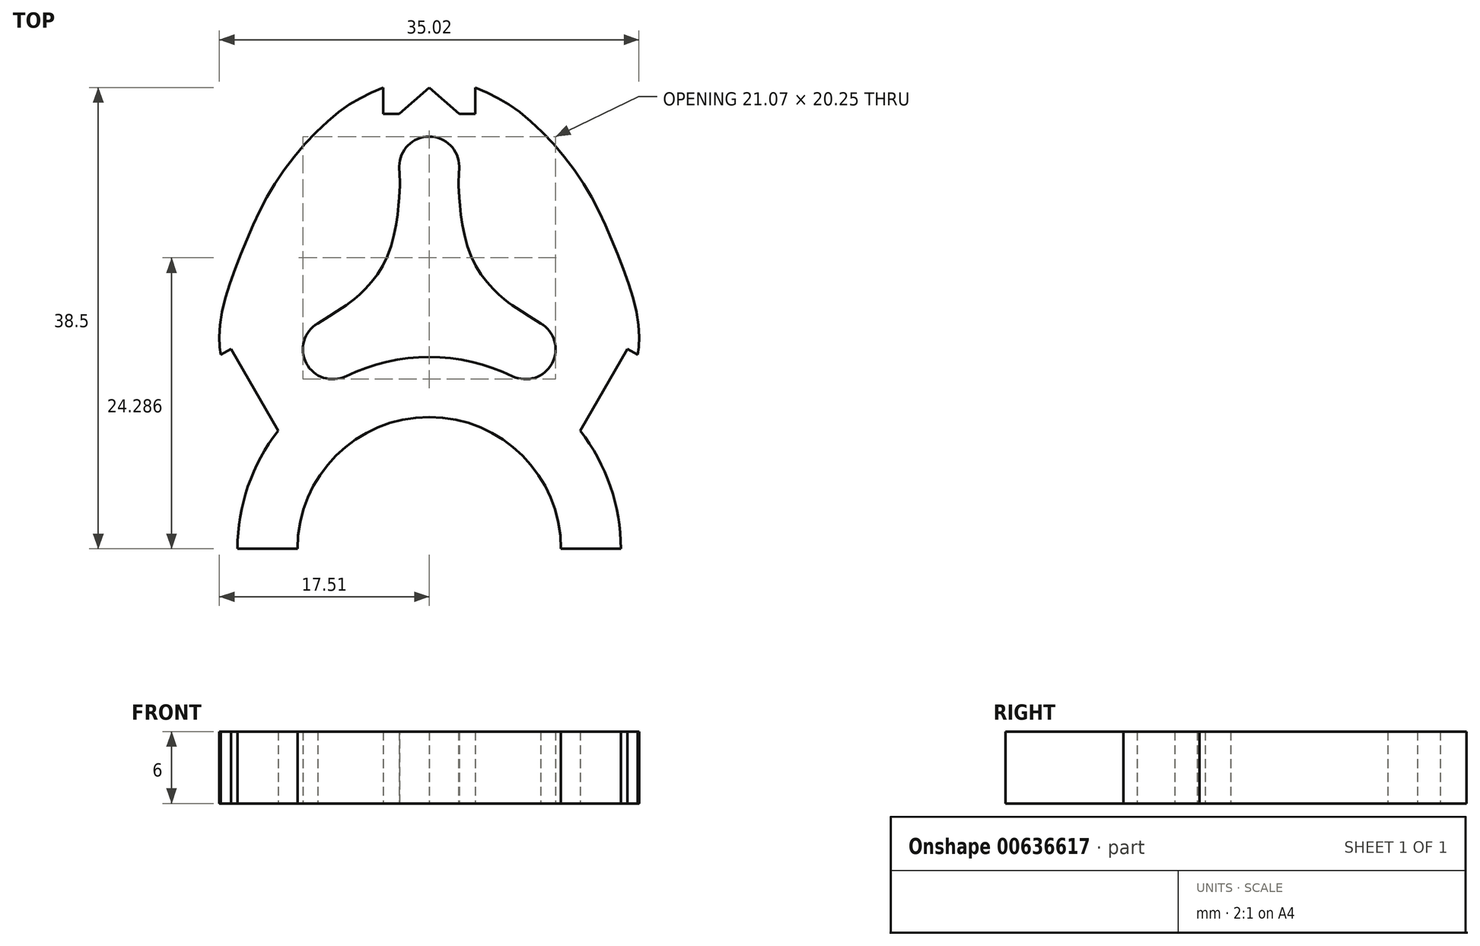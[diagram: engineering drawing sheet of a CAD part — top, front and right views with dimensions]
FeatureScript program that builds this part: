
annotation { "Feature Type Name" : "Feature", "Feature Type Description" : "" }
export const myFeature = defineFeature(function(context is Context, id is Id, definition is map)
    precondition{}
    {
        {
            var Q0;
            Q0=qCreatedBy(makeId("Top.planeOp"),FACE);
            var sketch = newSketch(context, id + "F0", { "sketchPlane" : qUnion([Q0])});
            skArc(sketch, "E0", {"start": v(16, 0) * mm, "mid": v(15.13, 5.21) * mm, "end": v(12.6, 9.86) * mm});
            skArc(sketch, "E1", {"start": v(11, 0) * mm, "mid": v(0, 11) * mm, "end": v(-11, 0) * mm});
            skLineSegment(sketch, "E2", {"start": v(0, 36.3) * mm, "end": v(0, 0) * mm, "construction": true});
            skLineSegment(sketch, "E3", {"start": v(3.84, 36.3) * mm, "end": v(2.52, 36.3) * mm});
            skLineSegment(sketch, "E4", {"start": v(16.55, 16.69) * mm, "end": v(17.41, 16.19) * mm});
            skFitSpline(sketch, "E5", {"points": [v(17.41, 16.19) * mm, v(17.41, 19.08) * mm, v(15.54, 25.05) * mm, v(12.52, 31.03) * mm, v(7.74, 36.3) * mm, v(3.84, 38.5) * mm], "startDerivative": vector(1.86, 12.58) * mm, "endDerivative": vector(-23.54, 9.7) * mm});
            skLineSegment(sketch, "E6", {"start": v(3.84, 38.5) * mm, "end": v(3.84, 36.3) * mm});
            skLineSegment(sketch, "E7.MirrorCS", {"start": v(-3.84, 36.3) * mm, "end": v(-2.52, 36.3) * mm});
            skLineSegment(sketch, "E8.MirrorCS", {"start": v(-16.55, 16.69) * mm, "end": v(-17.41, 16.19) * mm});
            skLineSegment(sketch, "E9.MirrorCS", {"start": v(-3.84, 38.5) * mm, "end": v(-3.84, 36.3) * mm});
            skFitSpline(sketch, "E10.MirrorCS", {"points": [v(-17.41, 16.19) * mm, v(-17.41, 19.08) * mm, v(-15.54, 25.05) * mm, v(-12.52, 31.03) * mm, v(-7.74, 36.3) * mm, v(-3.84, 38.5) * mm], "startDerivative": vector(-1.86, 12.58) * mm, "endDerivative": vector(23.54, 9.7) * mm});
            skLineSegment(sketch, "E11", {"start": v(-2.52, 36.3) * mm, "end": v(0, 38.5) * mm});
            skLineSegment(sketch, "E12.MirrorCS", {"start": v(2.52, 36.3) * mm, "end": v(0, 38.5) * mm});
            skArc(sketch, "E13", {"start": v(2.5, 31.9) * mm, "mid": v(0, 34.4) * mm, "end": v(-2.5, 31.9) * mm});
            skArc(sketch, "E14", {"start": v(-9.3, 18.82) * mm, "mid": v(-10.26, 15.48) * mm, "end": v(-6.96, 14.4) * mm});
            skArc(sketch, "E15.MirrorC", {"start": v(9.3, 18.82) * mm, "mid": v(10.26, 15.48) * mm, "end": v(6.96, 14.4) * mm});
            skCircle(sketch, "E16", {"center": v(0, 21.92) * mm, "radius": 3 * mm, "construction": true});
            skFitSpline(sketch, "E17", {"points": [v(-2.5, 31.9) * mm, v(-2.49, 29.65) * mm, v(-3.62, 24.11) * mm, v(-6.5, 20.64) * mm, v(-9.3, 18.82) * mm], "startDerivative": vector(1.05, -19.69) * mm, "endDerivative": vector(-25.78, -16.42) * mm});
            skFitSpline(sketch, "E18.MirrorCS", {"points": [v(2.5, 31.9) * mm, v(2.49, 29.65) * mm, v(3.62, 24.11) * mm, v(6.5, 20.64) * mm, v(9.3, 18.82) * mm], "startDerivative": vector(-1.05, -19.69) * mm, "endDerivative": vector(25.78, -16.42) * mm});
            skArc(sketch, "E19.trimOffspring", {"start": v(6.96, 14.4) * mm, "mid": v(0, 16) * mm, "end": v(-6.96, 14.4) * mm});
            skArc(sketch, "E20.trimOffspring", {"start": v(-12.6, 9.85) * mm, "mid": v(-15.13, 5.21) * mm, "end": v(-16, 0) * mm});
            skLineSegment(sketch, "E21.trimOffspring", {"start": v(-12.6, 9.85) * mm, "end": v(-16.55, 16.69) * mm});
            skLineSegment(sketch, "E22.trimOffspring", {"start": v(12.6, 9.86) * mm, "end": v(16.55, 16.69) * mm});
            skPoint(sketch, "E23.end.orphan", {"position": v(6.48, 0) * mm});
            skPoint(sketch, "E24.MirrorCS.start.orphan", {"position": v(-6.48, 0) * mm});
            skPoint(sketch, "E25.orphan", {"position": v(-7.05, 36.3) * mm});
            skPoint(sketch, "E26.end.orphan", {"position": v(7.05, 36.3) * mm});
            skPoint(sketch, "E27.orphan", {"position": v(0, 36.3) * mm});
            skLineSegment(sketch, "E28.MirrorCS", {"start": v(-12.6, 9.86) * mm, "end": v(-16.55, 16.69) * mm});
            skLineSegment(sketch, "E29.MirrorCS", {"start": v(12.6, 9.85) * mm, "end": v(16.55, 16.69) * mm});
            skArc(sketch, "E30.MirrorCS", {"start": v(-11, 0) * mm, "mid": v(0, 11) * mm, "end": v(11, 0) * mm});
            skArc(sketch, "E31.MirrorCS", {"start": v(-16, 0) * mm, "mid": v(-15.13, 5.21) * mm, "end": v(-12.6, 9.86) * mm});
            skArc(sketch, "E32.MirrorCS", {"start": v(-6.96, 14.4) * mm, "mid": v(0, 16) * mm, "end": v(6.96, 14.4) * mm});
            skFitSpline(sketch, "E33.MirrorCS", {"points": [v(17.41, 16.19) * mm, v(17.41, 19.08) * mm, v(15.54, 25.05) * mm, v(12.52, 31.03) * mm, v(7.74, 36.3) * mm, v(3.84, 38.5) * mm], "startDerivative": vector(1.86, 12.58) * mm, "endDerivative": vector(-23.54, 9.7) * mm});
            skArc(sketch, "E34.MirrorCS", {"start": v(-2.5, 31.9) * mm, "mid": v(0, 34.4) * mm, "end": v(2.5, 31.9) * mm});
            skArc(sketch, "E35.MirrorCS", {"start": v(12.6, 9.85) * mm, "mid": v(15.13, 5.21) * mm, "end": v(16, 0) * mm});
            skLineSegment(sketch, "E36", {"start": v(-16, 0) * mm, "end": v(-11, 0) * mm});
            skLineSegment(sketch, "E37", {"start": v(11, 0) * mm, "end": v(16, 0) * mm});
            skLineSegment(sketch, "E38", {"start": v(-15.14, 9.85) * mm, "end": v(15.05, 9.85) * mm, "construction": true});
            skSolve(sketch);
        }
        {
            var Q0;
            Q0=makeQuery(id+"F0.imprint","IMPRINT",FACE,{"disambiguationData":[TD([[makeQuery(id+"F0.imprint","IMPRINT",EDGE,{"derivedFrom":sQuery(id+"F0.wireOp",EDGE,"E7.MirrorCS")}),-1.0]])]});
            extrude(context, id + "F1", {"entities" : qUnion([Q0]), "depth" : 6 * mm, "offsetDistance" : 25 * mm});
        }
    });
